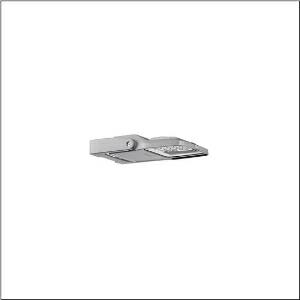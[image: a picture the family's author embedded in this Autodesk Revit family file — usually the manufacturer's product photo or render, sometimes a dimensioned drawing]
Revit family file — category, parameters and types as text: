
# Revit family: floodlight_fl_21_micro___pl52_5xa7762a4d2a_ae07
name_source: partatom
category: Lighting Fixtures
units: mm (PartAtom-declared; Revit-internal decimal feet)

## family parameters
Cut with Voids When Loaded = No
Host = Face
Light Source = No
Part Type = Normal
Room Calculation Point = No
Round Connector Dimension = Use Diameter
Shared = No

## types (1)
- --- (1 x LED, 3010 lm, 23.1 W, 4000K)
    Apparent Load = 23 VA
    CIE Flux Codes = 26 60 98 100 100
    Color Rendering = 70
    Color Temperature = 4000K
    Default Elevation = 1800 mm
    Description = Floodlight FL 21 micro, floodlight, primary light control with lens, of PMMA, primary optical cover: protective disc, of toughened safety glass, transparent, light distribution: PL52, light emission: direct distribution, installation type: surface-mounted, LED, High Power LED, rated luminous flux: 3.010lm, luminous efficacy: 130lm/W, light colour: 740, colour temperature: 4000K, control gear: ECG iQ, control: Auto-Match, Temp-Guard, Night-Set, Smart-Wire, Desk-Remote (wireless, voltage-free reading and setting of iQ features in the workshop via application-optimized NFC function/RFID function), optimised constant luminous flux control (CLO 2.0), Street-Remote, with terminal, 6-pole, mains connection: 220..240V, AC, 50/60Hz, start of lifetime: 23W, end of lifetime: 24W, reduction: 11W, luminaire housing, of diecast aluminium, powder-coated, Siteco® metallic grey (DB 702S), corrosivity category C5 according to DIN EN ISO 12944, design bracket, of diecast aluminium, powder-coated, Siteco® metallic grey (DB 702S), protection rating (complete): IP66, insulation class (complete): insulation class II (safety insulation), certification: CE, protection symbol: D, impact resistance: IK07, permissible operating ambient temperature: -40..+40°C, permissible operating ambient temperature for outdoor applications: -40..+50°C, standard: DIN EN 12944, packaging unit: 1 piece

Light Distribution: PL52
    Height = 65 mm
    Lamp = 1 x LED
    Lamp Light Flux = 3010 lm
    Lamp Power = 23.1 W
    Lamp count = 1
    Length = 312 mm
    Luminous efficacy = 130 lm/W
    Manufacturer = Siteco
    ModVariant = No
    Model = 5XA7762A4D2A
    Number of Poles = 1
    OnlyDefault = Yes
    Power Factor = 1
    Product Name = Floodlight FL 21 micro | PL52
    Product group = floodlight | pylon top
    ProductGroupID = 6101
    Protection Class = Protection class II
    Protection Degree = IP 66
    RLX_Detail_Level = 1
    RlxData = <blob elided: 97361 chars, md5=72e412f2>
    Socket = socket
    Standby Power = 0 W
    System Light Flux = 3010 lm
    System Power = 23 W
    Type Comments = factory setting: luminous flux: 100 % | dim-lin: 254 | 455 mA
    Type Image = l_1006878.jpg
    URL = http://relux.com
    VarID = @adj_090469
    Voltage = 0 V
    Weight = 0.00 kg
    Width = 230 mm

## geometry (parser evidence)
native form markers: Blend x4, Sweep x11
no freeform markers — native parametric forms only
